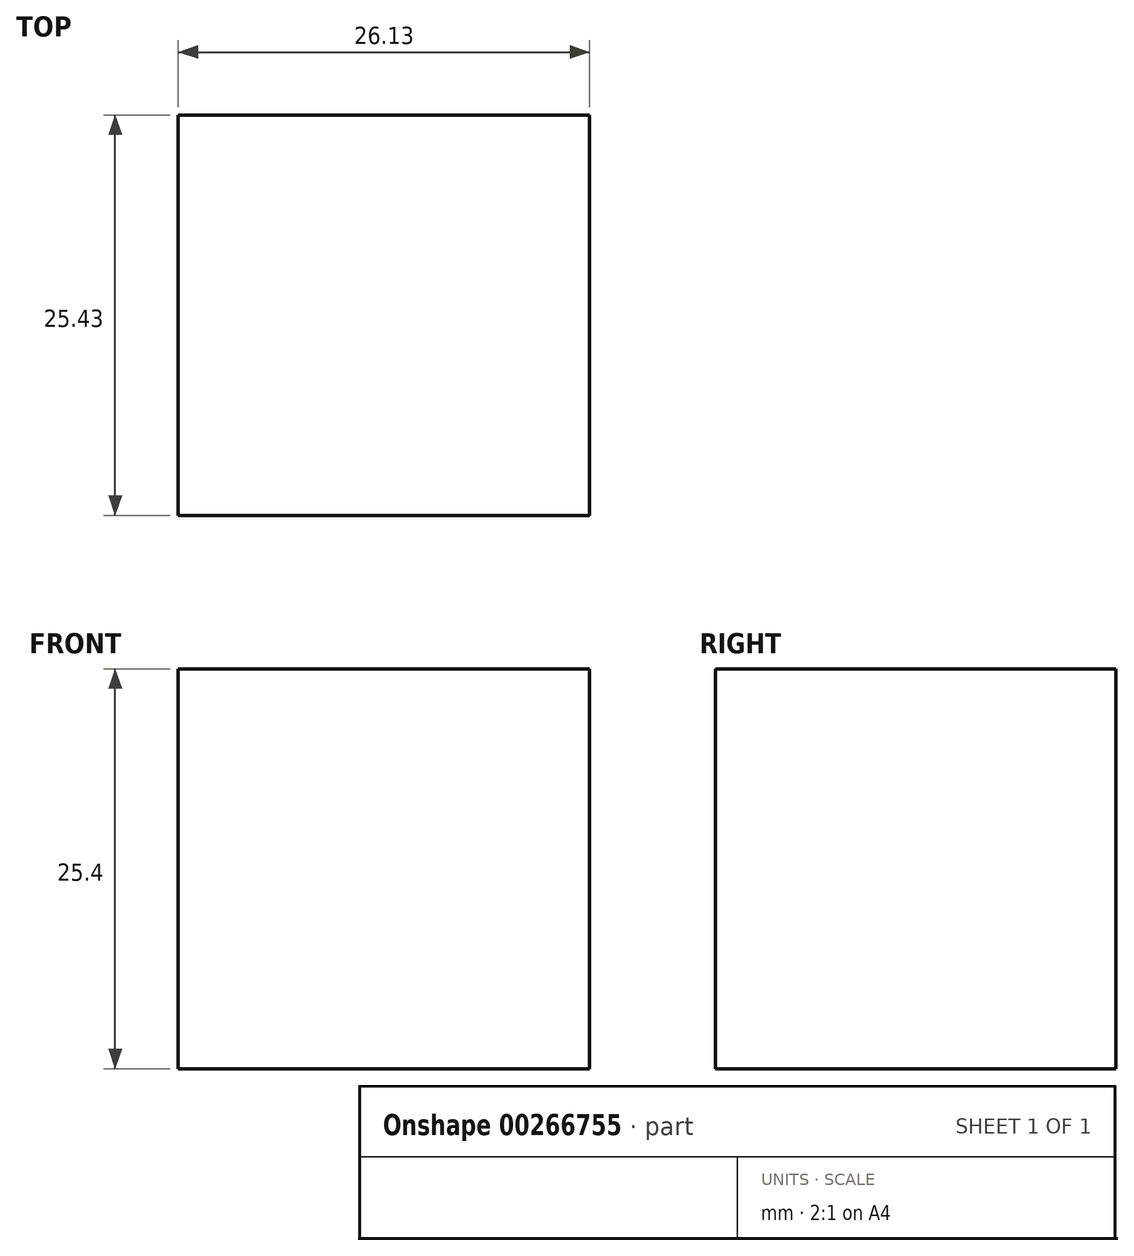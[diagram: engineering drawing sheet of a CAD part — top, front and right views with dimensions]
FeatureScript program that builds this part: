
annotation { "Feature Type Name" : "Feature", "Feature Type Description" : "" }
export const myFeature = defineFeature(function(context is Context, id is Id, definition is map)
    precondition{}
    {
        {
            var Q0;
            Q0=qCreatedBy(makeId("Top.planeOp"),FACE);
            var sketch = newSketch(context, id + "F0", { "sketchPlane" : qUnion([Q0])});
            skLineSegment(sketch, "E0.bottom", {"start": v(0, 0) * mm, "end": v(26.13, 0) * mm});
            skLineSegment(sketch, "E0.top", {"start": v(0, 25.43) * mm, "end": v(26.13, 25.43) * mm});
            skLineSegment(sketch, "E0.left", {"start": v(0, 0) * mm, "end": v(0, 25.43) * mm});
            skLineSegment(sketch, "E0.right", {"start": v(26.13, 0) * mm, "end": v(26.13, 25.43) * mm});
            skSolve(sketch);
        }
        {
            var Q0;
            Q0=makeQuery(id+"F0.imprint","IMPRINT",FACE,{"disambiguationData":[TD([[makeQuery(id+"F0.imprint","IMPRINT",EDGE,{"derivedFrom":sQuery(id+"F0.wireOp",EDGE,"E0.bottom")}),1.0]])]});
            extrude(context, id + "F1", {"entities" : qUnion([Q0]), "depth" : 25.4 * mm});
        }
    });
